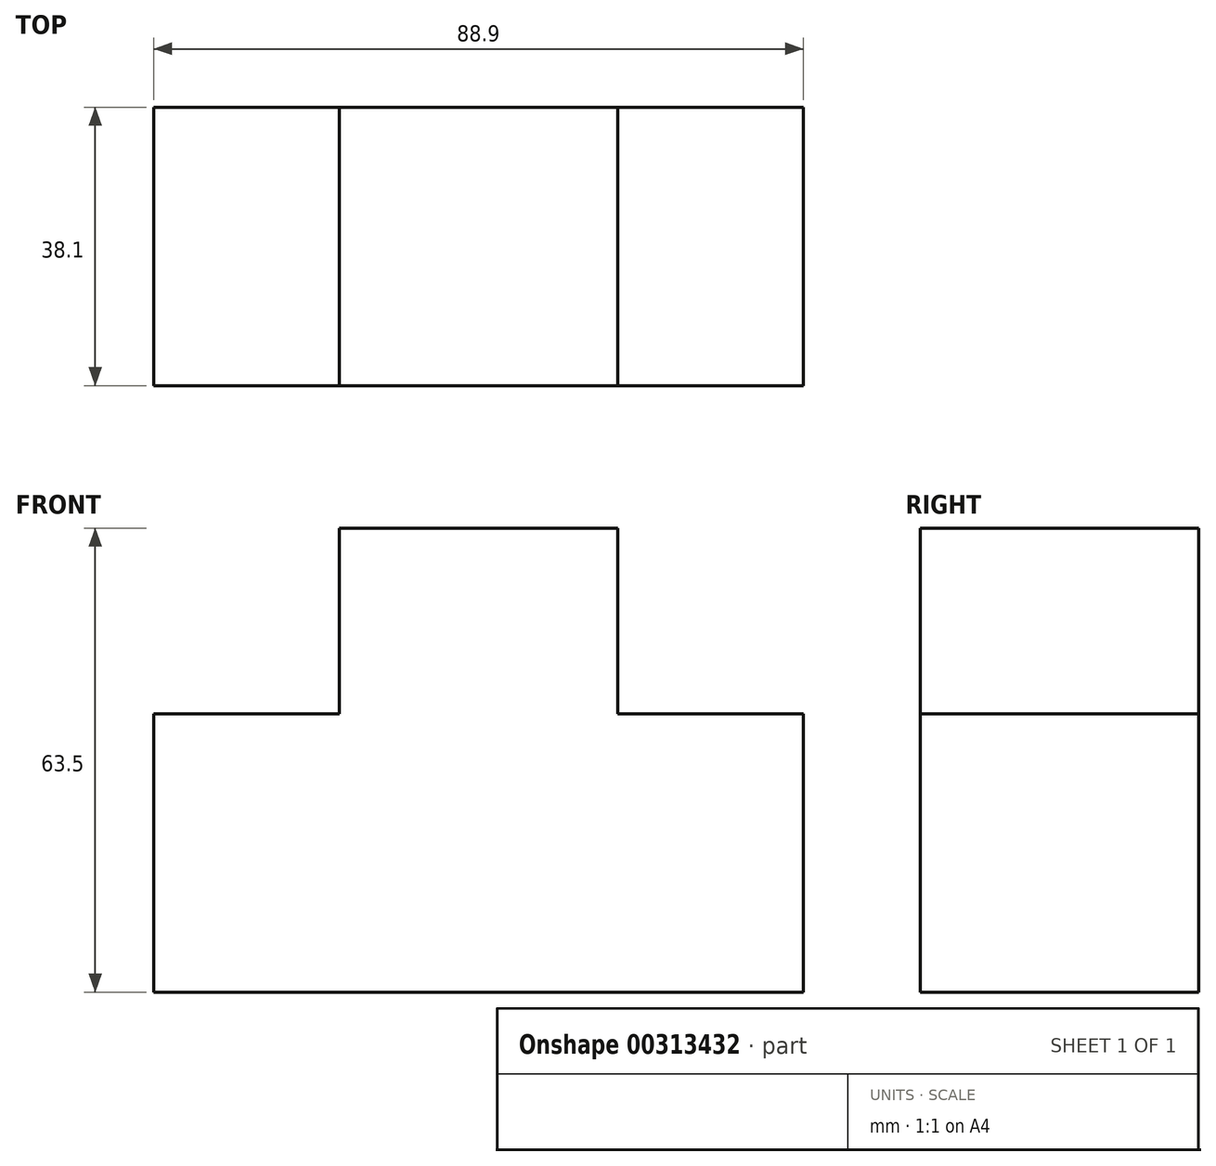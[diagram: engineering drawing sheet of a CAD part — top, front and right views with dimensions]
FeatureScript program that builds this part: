
annotation { "Feature Type Name" : "Feature", "Feature Type Description" : "" }
export const myFeature = defineFeature(function(context is Context, id is Id, definition is map)
    precondition{}
    {
        {
            var Q0;
            Q0=qCreatedBy(makeId("Front.planeOp"),FACE);
            var sketch = newSketch(context, id + "F0", { "sketchPlane" : qUnion([Q0])});
            skLineSegment(sketch, "E0", {"start": v(-51.01, -24.1) * mm, "end": v(37.89, -24.1) * mm});
            skLineSegment(sketch, "E1", {"start": v(37.89, -24.1) * mm, "end": v(37.89, 14) * mm});
            skLineSegment(sketch, "E2", {"start": v(37.89, 14) * mm, "end": v(12.49, 14) * mm});
            skLineSegment(sketch, "E3", {"start": v(12.49, 14) * mm, "end": v(12.49, 39.4) * mm});
            skLineSegment(sketch, "E4", {"start": v(12.49, 39.4) * mm, "end": v(-25.61, 39.4) * mm});
            skLineSegment(sketch, "E5", {"start": v(-25.61, 39.4) * mm, "end": v(-25.61, 14) * mm});
            skLineSegment(sketch, "E6", {"start": v(-25.61, 14) * mm, "end": v(-51.01, 14) * mm});
            skLineSegment(sketch, "E7", {"start": v(-51.01, 14) * mm, "end": v(-51.01, -24.1) * mm});
            skSolve(sketch);
        }
        {
            var Q0;
            Q0=makeQuery(id+"F0.imprint","IMPRINT",FACE,{"disambiguationData":[TD([[makeQuery(id+"F0.imprint","IMPRINT",EDGE,{"derivedFrom":sQuery(id+"F0.wireOp",EDGE,"E0")}),1.0]])]});
            extrude(context, id + "F1", {"entities" : qUnion([Q0]), "depth" : 38.1 * mm});
        }
    });
